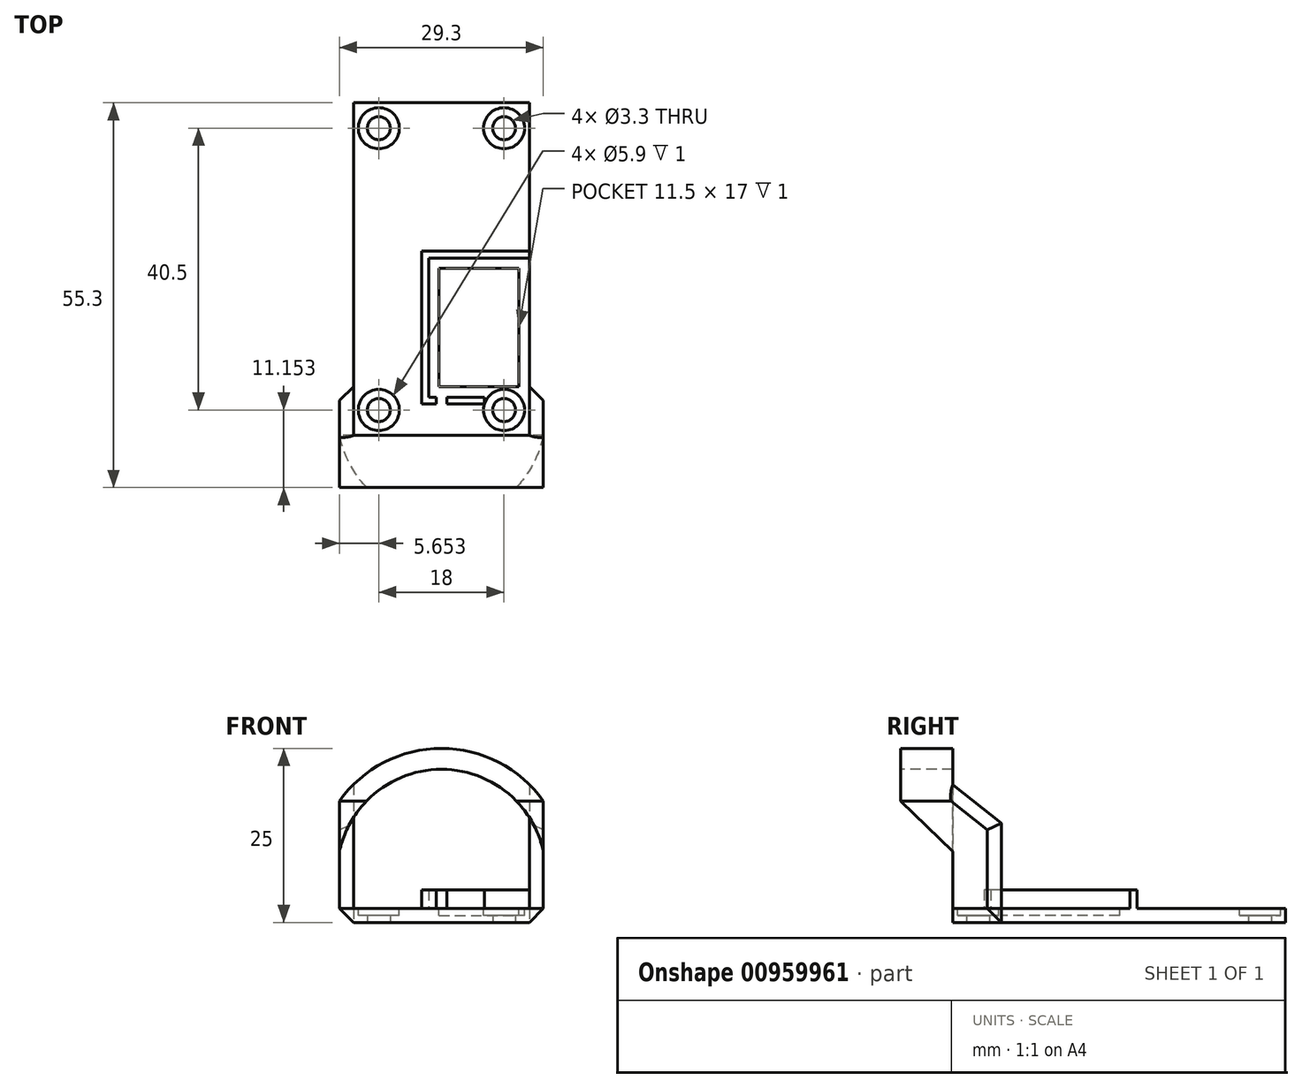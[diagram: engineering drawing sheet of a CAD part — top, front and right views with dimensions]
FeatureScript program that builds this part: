
annotation { "Feature Type Name" : "Feature", "Feature Type Description" : "" }
export const myFeature = defineFeature(function(context is Context, id is Id, definition is map)
    precondition{}
    {
        {
            var Q0;
            Q0=qCreatedBy(makeId("Top.planeOp"),FACE);
            var sketch = newSketch(context, id + "F0", { "sketchPlane" : qUnion([Q0])});
            skLineSegment(sketch, "E0.bottom", {"start": v(-22.44, 32.08) * mm, "end": v(2.86, 32.08) * mm});
            skLineSegment(sketch, "E0.top", {"start": v(-21.14, -15.72) * mm, "end": v(2.86, -15.72) * mm});
            skLineSegment(sketch, "E0.left", {"start": v(-22.44, 32.08) * mm, "end": v(-22.44, -8.72) * mm});
            skLineSegment(sketch, "E0.right", {"start": v(2.86, 32.08) * mm, "end": v(2.86, -8.72) * mm});
            skLineSegment(sketch, "E1", {"start": v(-21.79, -12.07) * mm, "end": v(2.86, -12.07) * mm, "construction": true});
            skPoint(sketch, "E2", {"position": v(-18.79, -12.07) * mm});
            skPoint(sketch, "E3", {"position": v(-0.79, -12.07) * mm});
            skCircle(sketch, "E4", {"center": v(-18.79, -12.07) * mm, "radius": 1.65 * mm});
            skCircle(sketch, "E5", {"center": v(-0.79, -12.07) * mm, "radius": 1.65 * mm});
            skLineSegment(sketch, "E6", {"start": v(2.86, -8.72) * mm, "end": v(4.86, -10.72) * mm});
            skLineSegment(sketch, "E7", {"start": v(4.86, -10.72) * mm, "end": v(4.86, -15.72) * mm});
            skLineSegment(sketch, "E8", {"start": v(4.86, -15.72) * mm, "end": v(2.86, -15.72) * mm});
            skLineSegment(sketch, "E9", {"start": v(-22.44, -8.72) * mm, "end": v(-24.44, -10.72) * mm});
            skLineSegment(sketch, "E10", {"start": v(-24.44, -10.72) * mm, "end": v(-24.44, -15.72) * mm});
            skLineSegment(sketch, "E11", {"start": v(-24.44, -15.72) * mm, "end": v(-21.14, -15.72) * mm});
            skCircle(sketch, "E12", {"center": v(-18.79, 28.43) * mm, "radius": 1.65 * mm});
            skCircle(sketch, "E13", {"center": v(-0.79, 28.43) * mm, "radius": 1.65 * mm});
            skSolve(sketch);
        }
        {
            var Q0;
            Q0=makeQuery(id+"F0.imprint","IMPRINT",FACE,{"disambiguationData":[TD([[makeQuery(id+"F0.imprint","IMPRINT",EDGE,{"derivedFrom":sQuery(id+"F0.wireOp",EDGE,"E0.bottom")}),-1.0]])]});
            extrude(context, id + "F1", {"entities" : qUnion([Q0]), "depth" : 2 * mm, "offsetDistance" : 25 * mm});
        }
        {
            var Q0;
            Q0=makeQuery(id+"F1.opExtrude","CAP_FACE",FACE,{"disambiguationData":[OSD([sQuery(id+"F0.wireOp",EDGE,"E0.bottom"),sQuery(id+"F0.wireOp",EDGE,"E0.top"),sQuery(id+"F0.wireOp",EDGE,"E0.left"),sQuery(id+"F0.wireOp",EDGE,"E0.right"),sQuery(id+"F0.wireOp",EDGE,"E4"),sQuery(id+"F0.wireOp",EDGE,"E5"),sQuery(id+"F0.wireOp",EDGE,"fuVWzpYH-3m4Q-cEJh-YOuV-TyPH2kjDz8uM.bottom"),sQuery(id+"F0.wireOp",EDGE,"fuVWzpYH-3m4Q-cEJh-YOuV-TyPH2kjDz8uM.top"),sQuery(id+"F0.wireOp",EDGE,"fuVWzpYH-3m4Q-cEJh-YOuV-TyPH2kjDz8uM.left"),sQuery(id+"F0.wireOp",EDGE,"SQc1fbUd-dRCy-1LRj-ip6P-61WSwEZlacvX")])],"isStart":false});
            var sketch = newSketch(context, id + "F2", { "sketchPlane" : qUnion([Q0])});
            skCircle(sketch, "E14", {"center": v(-18.79, -12.07) * mm, "radius": 2.95 * mm});
            skCircle(sketch, "E15", {"center": v(-0.79, -12.07) * mm, "radius": 2.95 * mm});
            skLineSegment(sketch, "E16.bottom", {"start": v(-22.44, 32.08) * mm, "end": v(2.86, 32.08) * mm});
            skLineSegment(sketch, "E16.top", {"start": v(-22.44, 32.08) * mm, "end": v(2.86, 32.08) * mm});
            skLineSegment(sketch, "E16.left", {"start": v(-22.44, 32.08) * mm, "end": v(-22.44, 32.08) * mm});
            skLineSegment(sketch, "E16.right", {"start": v(2.86, 32.08) * mm, "end": v(2.86, 32.08) * mm});
            skLineSegment(sketch, "E17.bottom", {"start": v(-10.14, 8.28) * mm, "end": v(1.36, 8.28) * mm});
            skLineSegment(sketch, "E17.top", {"start": v(-10.14, -8.72) * mm, "end": v(1.36, -8.72) * mm});
            skLineSegment(sketch, "E17.left", {"start": v(-10.14, 8.28) * mm, "end": v(-10.14, -8.72) * mm});
            skLineSegment(sketch, "E17.right", {"start": v(1.36, 8.28) * mm, "end": v(1.36, -8.72) * mm});
            skCircle(sketch, "E18", {"center": v(-18.79, 28.43) * mm, "radius": 2.95 * mm});
            skCircle(sketch, "E19", {"center": v(-0.79, 28.43) * mm, "radius": 2.95 * mm});
            skSolve(sketch);
        }
        {
            var Q0;
            Q0=makeQuery(id+"F2.imprint","IMPRINT",FACE,{"disambiguationData":[TD([[makeQuery(id+"F2.imprint","IMPRINT",EDGE,{"derivedFrom":sQuery(id+"F2.wireOp",EDGE,"E14")}),1.0]])]});
            var Q1;
            Q1=makeQuery(id+"F2.imprint","IMPRINT",FACE,{"disambiguationData":[TD([[makeQuery(id+"F2.imprint","IMPRINT",EDGE,{"derivedFrom":sQuery(id+"F2.wireOp",EDGE,"E15")}),1.0]])]});
            var Q2;
            Q2=makeQuery(id+"F2.imprint","IMPRINT",FACE,{"disambiguationData":[TD([[makeQuery(id+"F2.imprint","IMPRINT",EDGE,{"derivedFrom":sQuery(id+"F2.wireOp",EDGE,"E18")}),1.0]])]});
            var Q3;
            Q3=makeQuery(id+"F2.imprint","IMPRINT",FACE,{"disambiguationData":[TD([[makeQuery(id+"F2.imprint","IMPRINT",EDGE,{"derivedFrom":sQuery(id+"F2.wireOp",EDGE,"E19")}),1.0]])]});
            var Q4;
            Q4=makeQuery(id+"F2.imprint","IMPRINT",FACE,{"disambiguationData":[TD([[makeQuery(id+"F2.imprint","IMPRINT",EDGE,{"derivedFrom":sQuery(id+"F2.wireOp",EDGE,"E17.bottom")}),-1.0]])]});
            extrude(context, id + "F3", {"entities" : qUnion([Q0, Q1, Q2, Q3, Q4]), "operationType" : NewBodyOperationType.REMOVE, "oppositeDirection" : true, "depth" : 1 * mm, "offsetDistance" : 25 * mm});
        }
        {
            var Q0;
            Q0=makeQuery(id+"F1.opExtrude","CAP_FACE",FACE,{"disambiguationData":[OSD([sQuery(id+"F0.wireOp",EDGE,"E0.bottom"),sQuery(id+"F0.wireOp",EDGE,"E0.top"),sQuery(id+"F0.wireOp",EDGE,"E0.left"),sQuery(id+"F0.wireOp",EDGE,"E0.right"),sQuery(id+"F0.wireOp",EDGE,"E4"),sQuery(id+"F0.wireOp",EDGE,"E5"),sQuery(id+"F0.wireOp",EDGE,"fuVWzpYH-3m4Q-cEJh-YOuV-TyPH2kjDz8uM.bottom"),sQuery(id+"F0.wireOp",EDGE,"fuVWzpYH-3m4Q-cEJh-YOuV-TyPH2kjDz8uM.top"),sQuery(id+"F0.wireOp",EDGE,"fuVWzpYH-3m4Q-cEJh-YOuV-TyPH2kjDz8uM.left"),sQuery(id+"F0.wireOp",EDGE,"SQc1fbUd-dRCy-1LRj-ip6P-61WSwEZlacvX")])],"isStart":false});
            var sketch = newSketch(context, id + "F4", { "sketchPlane" : qUnion([Q0])});
            skLineSegment(sketch, "E20", {"start": v(-9.79, -15.72) * mm, "end": v(-9.79, -8.72) * mm, "construction": true});
            skLineSegment(sketch, "E21", {"start": v(-10.54, -10.22) * mm, "end": v(-10.54, -11.22) * mm});
            skLineSegment(sketch, "E22", {"start": v(-9.04, -10.22) * mm, "end": v(-9.04, -11.22) * mm});
            skLineSegment(sketch, "E23.bottom", {"start": v(-11.64, 9.78) * mm, "end": v(2.86, 9.78) * mm});
            skLineSegment(sketch, "E23.top", {"start": v(-11.64, -10.22) * mm, "end": v(-10.54, -10.22) * mm});
            skLineSegment(sketch, "E23.left", {"start": v(-11.64, 9.78) * mm, "end": v(-11.64, -10.22) * mm});
            skLineSegment(sketch, "E24.bottom", {"start": v(-10.14, 8.28) * mm, "end": v(1.36, 8.28) * mm, "construction": true});
            skLineSegment(sketch, "E24.top", {"start": v(-10.14, -8.72) * mm, "end": v(1.36, -8.72) * mm, "construction": true});
            skLineSegment(sketch, "E24.left", {"start": v(-10.14, 8.28) * mm, "end": v(-10.14, -8.72) * mm, "construction": true});
            skLineSegment(sketch, "E24.right", {"start": v(1.36, 8.28) * mm, "end": v(1.36, -8.72) * mm, "construction": true});
            skLineSegment(sketch, "E25", {"start": v(2.86, 32.08) * mm, "end": v(2.86, 32.08) * mm});
            skLineSegment(sketch, "E26", {"start": v(2.86, 9.78) * mm, "end": v(2.86, 10.78) * mm});
            skLineSegment(sketch, "E27", {"start": v(2.86, 10.78) * mm, "end": v(-12.64, 10.78) * mm});
            skLineSegment(sketch, "E28", {"start": v(-12.64, 10.78) * mm, "end": v(-12.64, -11.22) * mm});
            skLineSegment(sketch, "E29", {"start": v(-12.64, -11.22) * mm, "end": v(-10.54, -11.22) * mm});
            skLineSegment(sketch, "E30", {"start": v(-3.64, -11.22) * mm, "end": v(-3.64, -10.22) * mm});
            skLineSegment(sketch, "E31.trimOffspring", {"start": v(-9.04, -11.22) * mm, "end": v(-3.64, -11.22) * mm});
            skLineSegment(sketch, "E32.trimOffspring", {"start": v(-9.04, -10.22) * mm, "end": v(-3.64, -10.22) * mm});
            skSolve(sketch);
        }
        {
            var Q0;
            Q0=makeQuery(id+"F4.imprint","IMPRINT",FACE,{"disambiguationData":[TD([[makeQuery(id+"F4.imprint","IMPRINT",EDGE,{"derivedFrom":sQuery(id+"F4.wireOp",EDGE,"E21")}),-1.0]])]});
            var Q1;
            Q1=makeQuery(id+"F4.imprint","IMPRINT",FACE,{"disambiguationData":[TD([[makeQuery(id+"F4.imprint","IMPRINT",EDGE,{"derivedFrom":sQuery(id+"F4.wireOp",EDGE,"E22")}),1.0]])]});
            extrude(context, id + "F5", {"entities" : qUnion([Q0, Q1]), "operationType" : NewBodyOperationType.ADD, "depth" : 2.65 * mm, "offsetDistance" : 25 * mm});
        }
        {
            var Q0;
            Q0=makeQuery(id+"F1.opExtrude","CAP_FACE",FACE,{"disambiguationData":[OSD([sQuery(id+"F0.wireOp",EDGE,"E0.bottom"),sQuery(id+"F0.wireOp",EDGE,"E0.top"),sQuery(id+"F0.wireOp",EDGE,"E0.left"),sQuery(id+"F0.wireOp",EDGE,"E0.right"),sQuery(id+"F0.wireOp",EDGE,"E4"),sQuery(id+"F0.wireOp",EDGE,"E5"),sQuery(id+"F0.wireOp",EDGE,"fuVWzpYH-3m4Q-cEJh-YOuV-TyPH2kjDz8uM.bottom"),sQuery(id+"F0.wireOp",EDGE,"fuVWzpYH-3m4Q-cEJh-YOuV-TyPH2kjDz8uM.top"),sQuery(id+"F0.wireOp",EDGE,"fuVWzpYH-3m4Q-cEJh-YOuV-TyPH2kjDz8uM.left"),sQuery(id+"F0.wireOp",EDGE,"SQc1fbUd-dRCy-1LRj-ip6P-61WSwEZlacvX"),sQuery(id+"F0.wireOp",EDGE,"E6"),sQuery(id+"F0.wireOp",EDGE,"E7"),sQuery(id+"F0.wireOp",EDGE,"E8"),sQuery(id+"F0.wireOp",EDGE,"E9"),sQuery(id+"F0.wireOp",EDGE,"E10"),sQuery(id+"F0.wireOp",EDGE,"E11")])],"isStart":false});
            var sketch = newSketch(context, id + "F6", { "sketchPlane" : qUnion([Q0])});
            skLineSegment(sketch, "E33", {"start": v(2.86, -8.72) * mm, "end": v(4.86, -10.72) * mm});
            skLineSegment(sketch, "E34", {"start": v(4.86, -10.72) * mm, "end": v(4.86, -23.22) * mm});
            skLineSegment(sketch, "E35", {"start": v(4.86, -23.22) * mm, "end": v(-24.44, -23.22) * mm});
            skLineSegment(sketch, "E36", {"start": v(-24.44, -23.22) * mm, "end": v(-24.44, -10.72) * mm});
            skLineSegment(sketch, "E37", {"start": v(-24.44, -10.72) * mm, "end": v(-22.44, -8.72) * mm});
            skLineSegment(sketch, "E38", {"start": v(-22.44, -8.72) * mm, "end": v(-22.44, -15.72) * mm});
            skLineSegment(sketch, "E39", {"start": v(-22.44, -15.72) * mm, "end": v(2.86, -15.72) * mm});
            skLineSegment(sketch, "E40", {"start": v(2.86, -15.72) * mm, "end": v(2.86, -8.72) * mm});
            skSolve(sketch);
        }
        {
            var Q0;
            {var subQ3=sQuery(id+"F6.wireOp",EDGE,"E35");Q0=makeQuery(id+"F6.imprint","IMPRINT",FACE,{"disambiguationData":[TD([[makeQuery(id+"F6.imprint","IMPRINT",EDGE,{"derivedFrom":subQ3}),-1.0]])]});}
            var Q1;
            {var subQ0=sQuery(id+"F6.wireOp",EDGE,"E33");Q1=makeQuery(id+"F6.imprint","IMPRINT",FACE,{"disambiguationData":[TD([[makeQuery(id+"F6.imprint","IMPRINT",EDGE,{"derivedFrom":subQ0}),-1.0]])]});}
            var Q2;
            {var subQ0=sQuery(id+"F6.wireOp",EDGE,"E37");Q2=makeQuery(id+"F6.imprint","IMPRINT",FACE,{"disambiguationData":[TD([[makeQuery(id+"F6.imprint","IMPRINT",EDGE,{"derivedFrom":subQ0}),1.0]])]});}
            extrude(context, id + "F7", {"entities" : qUnion([Q0, Q1, Q2]), "depth" : 23 * mm, "offsetDistance" : 25 * mm});
        }
        {
            var Q0;
            Q0=makeQuery(id+"F7.opExtrude","SWEPT_FACE",FACE,{"disambiguationData":[OSD([sQuery(id+"F6.wireOp",EDGE,"E35")])]});
            var sketch = newSketch(context, id + "F8", { "sketchPlane" : qUnion([Q0])});
            skArc(sketch, "E41", {"start": v(4.86, 10.22) * mm, "mid": v(-9.79, 22) * mm, "end": v(-24.44, 10.22) * mm});
            skLineSegment(sketch, "E42.bottom", {"start": v(-24.44, 25) * mm, "end": v(4.86, 25) * mm});
            skLineSegment(sketch, "E42.top", {"start": v(-24.44, 2) * mm, "end": v(4.86, 2) * mm});
            skLineSegment(sketch, "E42.left", {"start": v(-24.44, 25) * mm, "end": v(-24.44, 17.46) * mm});
            skLineSegment(sketch, "E42.right", {"start": v(4.86, 25) * mm, "end": v(4.86, 17.46) * mm});
            skLineSegment(sketch, "E43.trimOffspring", {"start": v(-24.44, 10.22) * mm, "end": v(-24.44, 2) * mm});
            skLineSegment(sketch, "E44.trimOffspring", {"start": v(4.86, 10.22) * mm, "end": v(4.86, 2) * mm});
            skArc(sketch, "E45", {"start": v(4.86, 17.46) * mm, "mid": v(-9.79, 25) * mm, "end": v(-24.44, 17.46) * mm});
            skSolve(sketch);
        }
        {
            var Q0;
            Q0=makeQuery(id+"F8.imprint","IMPRINT",FACE,{"disambiguationData":[TD([[makeQuery(id+"F8.imprint","IMPRINT",EDGE,{"derivedFrom":sQuery(id+"F8.wireOp",EDGE,"E41")}),1.0]])]});
            extrude(context, id + "F9", {"entities" : qUnion([Q0]), "operationType" : NewBodyOperationType.REMOVE, "oppositeDirection" : true, "depth" : 7.5 * mm, "offsetDistance" : 25 * mm});
        }
        {
            var Q0;
            {var subQ0=sQuery(id+"F8.wireOp",EDGE,"E42.left");Q0=makeQuery(id+"F8.imprint","IMPRINT",FACE,{"disambiguationData":[TD([[makeQuery(id+"F8.imprint","IMPRINT",EDGE,{"derivedFrom":subQ0}),1.0]])]});}
            var Q1;
            {var subQ0=sQuery(id+"F8.wireOp",EDGE,"E42.right");Q1=makeQuery(id+"F8.imprint","IMPRINT",FACE,{"disambiguationData":[TD([[makeQuery(id+"F8.imprint","IMPRINT",EDGE,{"derivedFrom":subQ0}),-1.0]])]});}
            extrude(context, id + "F10", {"entities" : qUnion([Q0, Q1]), "operationType" : NewBodyOperationType.REMOVE, "endBound" : BoundingType.THROUGH_ALL, "oppositeDirection" : true, "depth" : 25 * mm, "offsetDistance" : 25 * mm});
        }
        {
            var Q0;
            Q0=makeQuery(id+"F7.opExtrude","SWEPT_FACE",FACE,{"disambiguationData":[OSD([sQuery(id+"F6.wireOp",EDGE,"E34")])]});
            var sketch = newSketch(context, id + "F11", { "sketchPlane" : qUnion([Q0])});
            skLineSegment(sketch, "E46", {"start": v(-15.72, 10.22) * mm, "end": v(-23.22, 10.22) * mm});
            skLineSegment(sketch, "E47", {"start": v(-23.22, 10.22) * mm, "end": v(-23.22, 17.46) * mm});
            skLineSegment(sketch, "E48", {"start": v(-23.22, 17.46) * mm, "end": v(-15.72, 10.22) * mm});
            skSolve(sketch);
        }
        {
            var Q0;
            Q0=makeQuery(id+"F11.imprint","IMPRINT",FACE,{"disambiguationData":[TD([[makeQuery(id+"F11.imprint","IMPRINT",EDGE,{"derivedFrom":sQuery(id+"F11.wireOp",EDGE,"E46")}),-1.0]])]});
            extrude(context, id + "F12", {"entities" : qUnion([Q0]), "operationType" : NewBodyOperationType.REMOVE, "endBound" : BoundingType.THROUGH_ALL, "oppositeDirection" : true, "depth" : 25 * mm, "offsetDistance" : 25 * mm});
        }
        {
            var Q0;
            Q0=makeQuery(id+"F1.opExtrude","CAP_EDGE",EDGE,{"disambiguationData":[OSD([sQuery(id+"F0.wireOp",EDGE,"E7")])],"isStart":true});
            var Q1;
            Q1=makeQuery(id+"F1.opExtrude","CAP_EDGE",EDGE,{"disambiguationData":[OSD([sQuery(id+"F0.wireOp",EDGE,"E10")])],"isStart":true});
            chamfer(context, id + "F13", {"entities" : qUnion([Q0, Q1]), "width" : 2 * mm, "tangentPropagation" : true});
        }
        {
            var Q0;
            Q0=makeQuery(id+"F7.opExtrude","SWEPT_FACE",FACE,{"disambiguationData":[OSD([sQuery(id+"F6.wireOp",EDGE,"E38")])]});
            var sketch = newSketch(context, id + "F14", { "sketchPlane" : qUnion([Q0])});
            skLineSegment(sketch, "E49", {"start": v(-15.72, 19.8) * mm, "end": v(-8.72, 14.27) * mm});
            skLineSegment(sketch, "E50", {"start": v(-8.72, 14.27) * mm, "end": v(-8.72, 19.8) * mm});
            skLineSegment(sketch, "E51", {"start": v(-8.72, 19.8) * mm, "end": v(-15.72, 19.8) * mm});
            skSolve(sketch);
        }
        {
            var Q0;
            Q0=makeQuery(id+"F14.imprint","IMPRINT",FACE,{"disambiguationData":[TD([[makeQuery(id+"F14.imprint","IMPRINT",EDGE,{"derivedFrom":sQuery(id+"F14.wireOp",EDGE,"E49")}),1.0]])]});
            extrude(context, id + "F15", {"entities" : qUnion([Q0]), "operationType" : NewBodyOperationType.REMOVE, "endBound" : BoundingType.THROUGH_ALL, "oppositeDirection" : true, "depth" : 25 * mm, "offsetDistance" : 25 * mm});
        }
        {
            var Q0;
            Q0=makeQuery(id+"F7.opExtrude","SWEPT_FACE",FACE,{"disambiguationData":[OSD([sQuery(id+"F6.wireOp",EDGE,"E40")])]});
            var sketch = newSketch(context, id + "F16", { "sketchPlane" : qUnion([Q0])});
            skLineSegment(sketch, "E52", {"start": v(8.72, 19.8) * mm, "end": v(15.72, 19.8) * mm});
            skLineSegment(sketch, "E53", {"start": v(15.72, 19.8) * mm, "end": v(8.72, 14.27) * mm});
            skLineSegment(sketch, "E54", {"start": v(8.72, 14.27) * mm, "end": v(8.72, 19.8) * mm});
            skSolve(sketch);
        }
        {
            var Q0;
            Q0=makeQuery(id+"F16.imprint","IMPRINT",FACE,{"disambiguationData":[TD([[makeQuery(id+"F16.imprint","IMPRINT",EDGE,{"derivedFrom":sQuery(id+"F16.wireOp",EDGE,"E52")}),1.0]])]});
            extrude(context, id + "F17", {"entities" : qUnion([Q0]), "operationType" : NewBodyOperationType.REMOVE, "endBound" : BoundingType.THROUGH_ALL, "oppositeDirection" : true, "depth" : 25 * mm, "offsetDistance" : 25 * mm});
        }
        {
            var Q0;
            Q0=makeQuery(id+"F15.boolean.opBoolean","INTERSECT",EDGE,{"derivedFrom":[makeQuery(id+"F7.opExtrude","SWEPT_FACE",FACE,{"disambiguationData":[OSD([sQuery(id+"F6.wireOp",EDGE,"E36")])]}),makeQuery(id+"F15.opExtrude","SWEPT_FACE",FACE,{"disambiguationData":[OSD([sQuery(id+"F14.wireOp",EDGE,"E49")])]})]});
            var Q1;
            Q1=makeQuery(id+"F17.boolean.opBoolean","INTERSECT",EDGE,{"derivedFrom":[makeQuery(id+"F7.opExtrude","SWEPT_FACE",FACE,{"disambiguationData":[OSD([sQuery(id+"F6.wireOp",EDGE,"E34")])]}),makeQuery(id+"F17.opExtrude","SWEPT_FACE",FACE,{"disambiguationData":[OSD([sQuery(id+"F16.wireOp",EDGE,"E53")])]})]});
            chamfer(context, id + "F18", {"entities" : qUnion([Q0, Q1]), "width" : 2 * mm, "tangentPropagation" : true});
        }
    });
